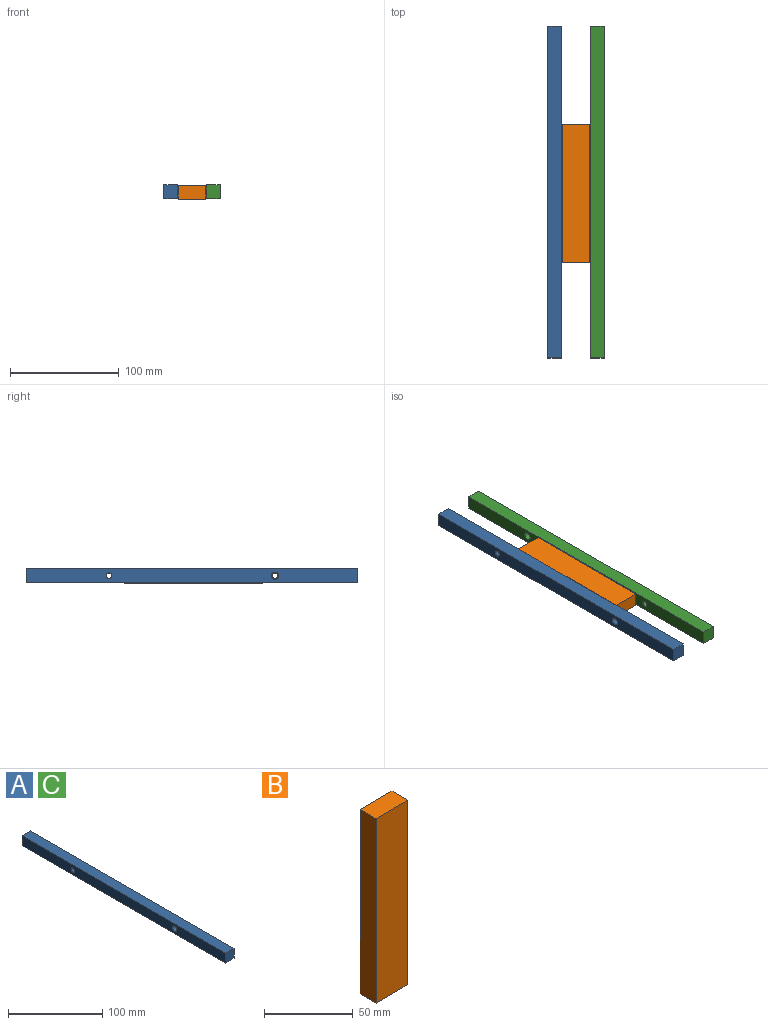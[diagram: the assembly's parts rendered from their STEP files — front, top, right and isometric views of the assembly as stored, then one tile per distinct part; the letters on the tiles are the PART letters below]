
ASSEMBLY  parts=3 mates=3
PART A: 8 faces, bbox 12.7x304.8x12.7 mm
  f0: plane 304.8x12.7mm, normal (0,0,1), area 3871mm2, adj f1,f3,f4,f5
  f1: plane 304.8x12.7mm, normal (-1,0,0), area 3814.6mm2, adj f0,f2,f4,f5,f6,f7
  f2: plane 304.8x12.7mm, normal (0,0,-1), area 3871mm2, adj f1,f3,f4,f5
  f3: plane 304.8x12.7mm, normal (1,0,0), area 3814.6mm2, adj f0,f2,f4,f5,f6,f7
  f4: plane 12.7x12.7mm, normal (0,-1,0), area 161.3mm2, adj f0,f1,f2,f3
  f5: plane 12.7x12.7mm, normal (0,1,0), area 161.3mm2, adj f0,f1,f2,f3
  f6: cylinder r=3.38mm len=12.7mm, axis (1,0,0), area 269.6mm2, adj f1,f3
  f7: cylinder r=2.55mm len=12.7mm, axis (1,0,0), area 203.7mm2, adj f1,f3
PART B: 13 faces, bbox 25.4x12.7x127 mm
  f0: plane 127x25.4mm, normal (0,1,0), area 2975.8mm2, adj f1,f3,f4,f5,f6,f7,f8,f9
  f1: plane 127x12.7mm, normal (-1,0,0), area 1612.9mm2, adj f0,f2,f4,f5
  f2: plane 127x25.4mm, normal (0,-1,0), area 3225.8mm2, adj f1,f3,f4,f5
  f3: plane 127x12.7mm, normal (1,0,0), area 1612.9mm2, adj f0,f2,f4,f5
  f4: plane 25.4x12.7mm, normal (0,0,1), area 322.6mm2, adj f0,f1,f2,f3
  f5: plane 25.4x12.7mm, normal (0,0,-1), area 322.6mm2, adj f0,f1,f2,f3
  f6: plane 76.2x3.18mm, normal (-1,0,0), area 241.9mm2, adj f0,f7,f11,f12
  f7: plane 3.18x2.54mm, normal (-0.85,0,0.53), area 9.5mm2, adj f0,f6,f8,f12
  f8: plane 3.18x2.54mm, normal (0.85,0,0.53), area 9.5mm2, adj f0,f7,f9,f12
  f9: plane 76.2x3.18mm, normal (1,0,0), area 241.9mm2, adj f0,f8,f10,f12
  f10: plane 3.18x2.54mm, normal (0.85,0,-0.53), area 9.5mm2, adj f0,f9,f11,f12
  f11: plane 3.18x2.54mm, normal (-0.85,0,-0.53), area 9.5mm2, adj f0,f6,f10,f12
  f12: plane 81.28x3.18mm, normal (0,1,0), area 250mm2, adj f6,f7,f8,f9,f10,f11
PART C: same geometry as A
PLACE A t=(-1.43,-156.34,-64.72)mm
PLACE B rot(axis=(-1,0,0),90deg) t=(11.9,-373.78,-52.59)mm
PLACE C rot(axis=(1,0,0),180deg) t=(37.64,-461.14,-52.02)mm
MATE parallel B.f0 <-> A.f0  axis (0,0,-1) through (26.06,-310.28,-65.29)mm
MATE cylindrical C.f7 <-> A.f6  axis (1,0,0) through (50.34,-384.94,-58.37)mm
MATE cylindrical A.f7 <-> C.f6  axis (1,0,0) through (11.27,-232.54,-58.37)mm
